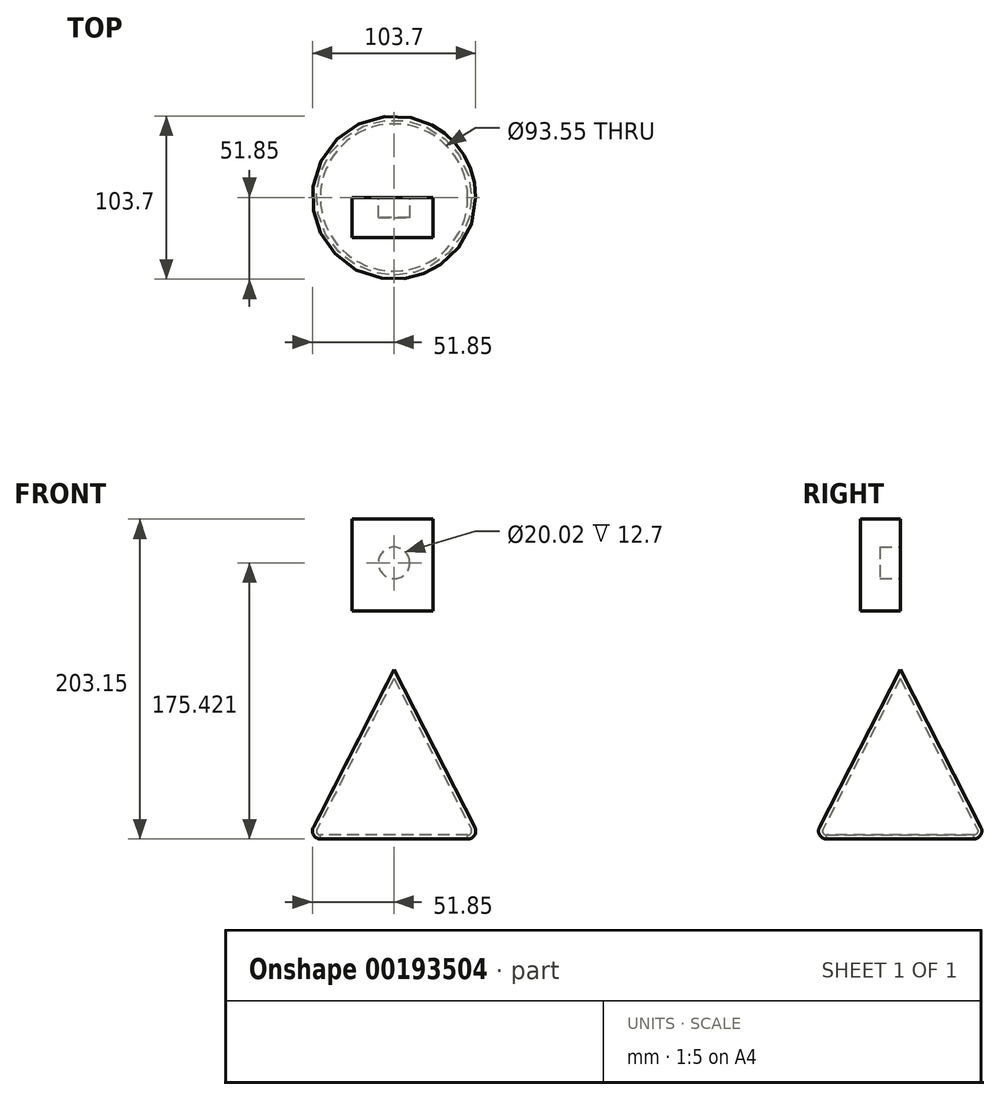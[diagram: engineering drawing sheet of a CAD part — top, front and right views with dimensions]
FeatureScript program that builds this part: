
annotation { "Feature Type Name" : "Feature", "Feature Type Description" : "" }
export const myFeature = defineFeature(function(context is Context, id is Id, definition is map)
    precondition{}
    {
        {
            var Q0;
            Q0=qCreatedBy(makeId("Front.planeOp"),FACE);
            var sketch = newSketch(context, id + "F0", { "sketchPlane" : qUnion([Q0])});
            skLineSegment(sketch, "E0", {"start": v(0, 49.27) * mm, "end": v(0, -58.36) * mm});
            skLineSegment(sketch, "E1", {"start": v(0, -58.36) * mm, "end": v(55.08, -58.36) * mm});
            skLineSegment(sketch, "E2", {"start": v(55.08, -58.36) * mm, "end": v(0, 49.27) * mm});
            skSolve(sketch);
        }
        {
            var Q0;
            Q0=makeQuery(id+"F0.imprint","IMPRINT",FACE,{"disambiguationData":[TD([[makeQuery(id+"F0.imprint","IMPRINT",EDGE,{"derivedFrom":sQuery(id+"F0.wireOp",EDGE,"E0")}),1.0]])]});
            var Q1;
            Q1=sQuery(id+"F0.wireOp",EDGE,"E0");
            revolve(context, id + "F1", {"entities" : qUnion([Q0]), "axis" : qUnion([Q1]), "revolveType" : RevolveType.FULL});
        }
        {
            var Q0;
            Q0=qCreatedBy(makeId("Front.planeOp"),FACE);
            var sketch = newSketch(context, id + "F2", { "sketchPlane" : qUnion([Q0])});
            skLineSegment(sketch, "E3.bottom", {"start": v(-26.67, 144.79) * mm, "end": v(24.67, 144.79) * mm});
            skLineSegment(sketch, "E3.top", {"start": v(-26.67, 86.63) * mm, "end": v(24.67, 86.63) * mm});
            skLineSegment(sketch, "E3.left", {"start": v(-26.67, 144.79) * mm, "end": v(-26.67, 86.63) * mm});
            skLineSegment(sketch, "E3.right", {"start": v(24.67, 144.79) * mm, "end": v(24.67, 86.63) * mm});
            skSolve(sketch);
        }
        {
            var Q0;
            Q0=makeQuery(id+"F2.imprint","IMPRINT",FACE,{"disambiguationData":[TD([[makeQuery(id+"F2.imprint","IMPRINT",EDGE,{"derivedFrom":sQuery(id+"F2.wireOp",EDGE,"E3.bottom")}),-1.0]])]});
            extrude(context, id + "F3", {"entities" : qUnion([Q0]), "depth" : 25.4 * mm});
        }
        {
            var Q0;
            Q0=makeQuery(id+"F3.opExtrude","CAP_FACE",FACE,{"disambiguationData":[OSD([sQuery(id+"F2.wireOp",EDGE,"E3.bottom"),sQuery(id+"F2.wireOp",EDGE,"E3.top"),sQuery(id+"F2.wireOp",EDGE,"E3.left"),sQuery(id+"F2.wireOp",EDGE,"E3.right")])],"isStart":true});
            var sketch = newSketch(context, id + "F4", { "sketchPlane" : qUnion([Q0])});
            skSolve(sketch);
        }
        {
            var Q0;
            Q0=makeQuery(id+"F4.imprint","IMPRINT",FACE,{"disambiguationData":[TD([[makeQuery(id+"F4.imprint","IMPRINT",EDGE,{"derivedFrom":makeQuery(id+"F3.opExtrude","CAP_EDGE",EDGE,{"disambiguationData":[OSD([sQuery(id+"F2.wireOp",EDGE,"E3.bottom")])],"isStart":true})}),1.0]])]});
            var sketch = newSketch(context, id + "F5", { "sketchPlane" : qUnion([Q0])});
            skCircle(sketch, "E4", {"center": v(0, 117.06) * mm, "radius": 10.01 * mm});
            skSolve(sketch);
        }
        {
            var Q0;
            Q0 = qSketchRegion(id + "F5", true);
            extrude(context, id + "F6", {"entities" : qUnion([Q0]), "operationType" : NewBodyOperationType.REMOVE, "oppositeDirection" : true, "depth" : 12.7 * mm});
        }
        {
            var Q0;
            Q0=makeQuery(id+"F1.opRevolve","SWEPT_FACE",FACE,{"disambiguationData":[OSD([sQuery(id+"F0.wireOp",EDGE,"E1")])]});
            fillet(context, id + "F7", {"entities" : qUnion([Q0]), "radius" : 5.08 * mm, "tangentPropagation" : true, "allowEdgeOverflow" : false});
        }
        {
            var Q0;
            Q0=makeQuery(id+"F1.opRevolve","SWEPT_FACE",FACE,{"disambiguationData":[OSD([sQuery(id+"F0.wireOp",EDGE,"E1")])]});
            shell(context, id + "F8", {"entities" : qUnion([Q0]), "thickness" : 2.54 * mm});
        }
    });
